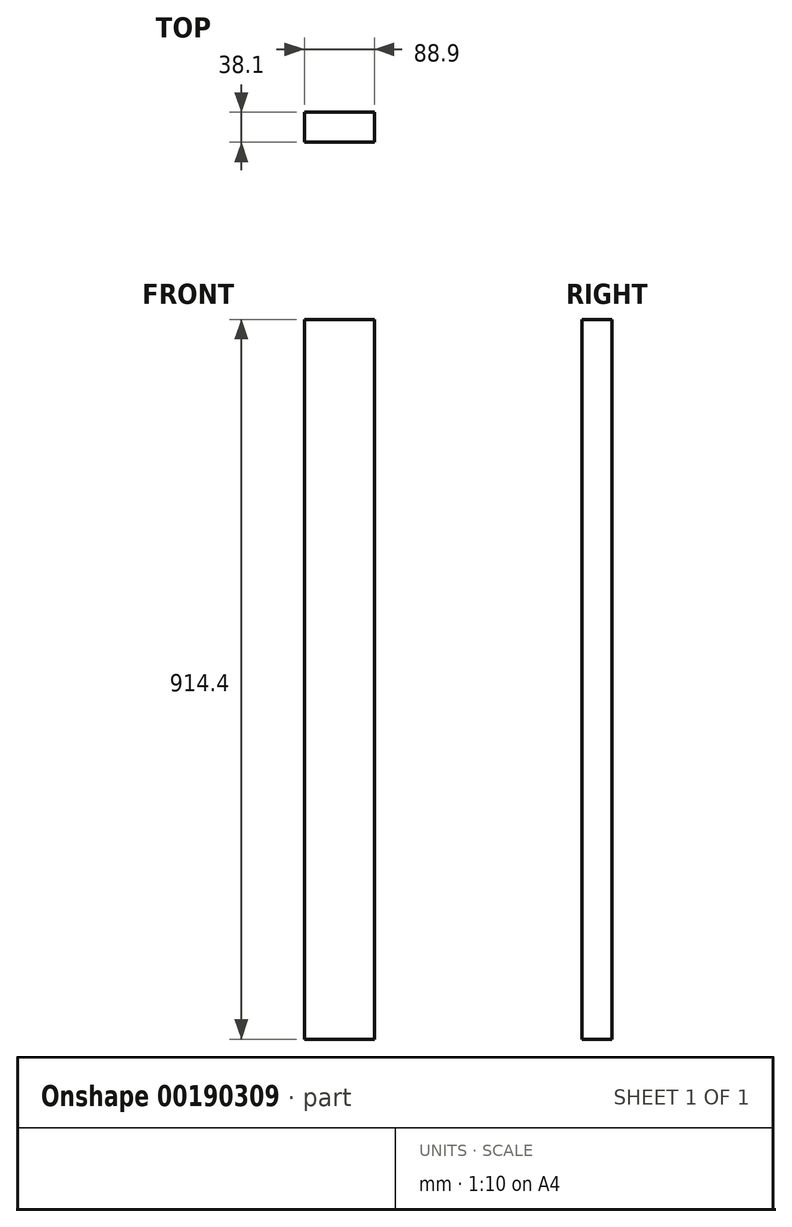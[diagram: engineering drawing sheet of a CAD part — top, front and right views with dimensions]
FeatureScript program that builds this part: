
annotation { "Feature Type Name" : "Feature", "Feature Type Description" : "" }
export const myFeature = defineFeature(function(context is Context, id is Id, definition is map)
    precondition{}
    {
        {
            var Q0;
            Q0=qCreatedBy(makeId("Top.planeOp"),FACE);
            var sketch = newSketch(context, id + "F0", { "sketchPlane" : qUnion([Q0])});
            skLineSegment(sketch, "E0.bottom", {"start": v(44.45, -19.05) * mm, "end": v(-44.45, -19.05) * mm});
            skLineSegment(sketch, "E0.top", {"start": v(44.45, 19.05) * mm, "end": v(-44.45, 19.05) * mm});
            skLineSegment(sketch, "E0.left", {"start": v(44.45, -19.05) * mm, "end": v(44.45, 19.05) * mm});
            skLineSegment(sketch, "E0.right", {"start": v(-44.45, -19.05) * mm, "end": v(-44.45, 19.05) * mm});
            skPoint(sketch, "E0.middle", {"position": v(0, 0) * mm});
            skSolve(sketch);
        }
        {
            var Q0;
            Q0=makeQuery(id+"F0.imprint","IMPRINT",FACE,{"disambiguationData":[TD([[makeQuery(id+"F0.imprint","IMPRINT",EDGE,{"derivedFrom":sQuery(id+"F0.wireOp",EDGE,"E0.bottom")}),-1.0]])]});
            extrude(context, id + "F1", {"entities" : qUnion([Q0]), "depth" : 914.4 * mm});
        }
    });
